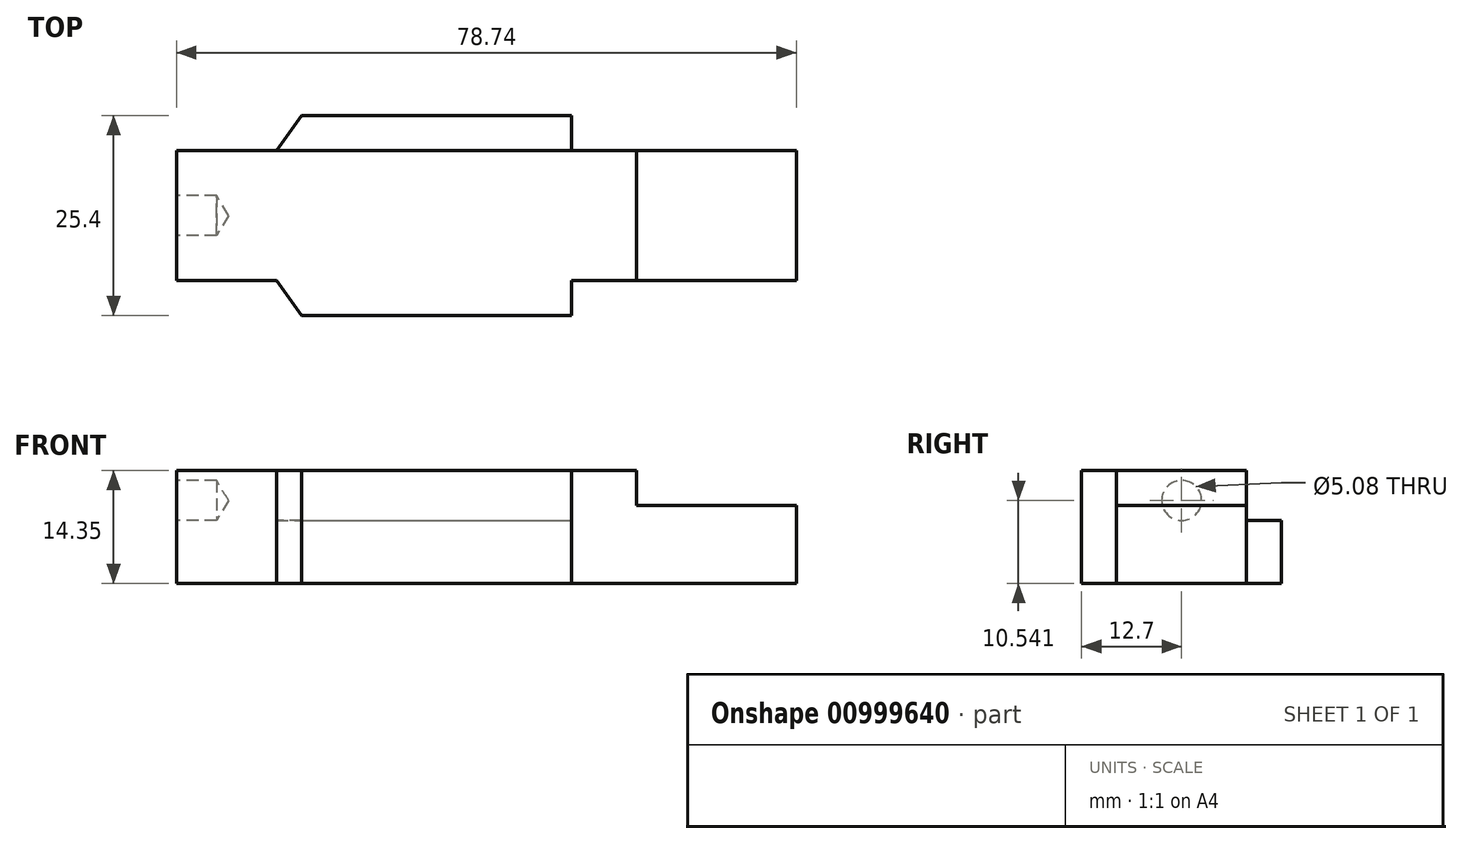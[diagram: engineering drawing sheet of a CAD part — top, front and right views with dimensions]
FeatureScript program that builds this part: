
annotation { "Feature Type Name" : "Feature", "Feature Type Description" : "" }
export const myFeature = defineFeature(function(context is Context, id is Id, definition is map)
    precondition{}
    {
        {
            var Q0;
            Q0=qCreatedBy(makeId("Front.planeOp"),FACE);
            var sketch = newSketch(context, id + "F0", { "sketchPlane" : qUnion([Q0])});
            skLineSegment(sketch, "E0", {"start": v(-39.37, 0) * mm, "end": v(-39.37, 14.35) * mm});
            skLineSegment(sketch, "E1", {"start": v(-39.37, 14.35) * mm, "end": v(19.05, 14.35) * mm});
            skLineSegment(sketch, "E2", {"start": v(19.05, 14.35) * mm, "end": v(19.05, 9.9) * mm});
            skLineSegment(sketch, "E3", {"start": v(19.05, 9.9) * mm, "end": v(39.37, 9.9) * mm});
            skLineSegment(sketch, "E4", {"start": v(39.37, 9.9) * mm, "end": v(39.37, 0) * mm});
            skLineSegment(sketch, "E5", {"start": v(39.37, 0) * mm, "end": v(-39.37, 0) * mm});
            skSolve(sketch);
        }
        {
            var Q0;
            Q0 = qSketchRegion(id + "F0", true);
            extrude(context, id + "F1", {"entities" : qUnion([Q0]), "depth" : 12.7 * mm, "offsetDistance" : 25.4 * mm, "hasSecondDirection" : true, "secondDirectionOppositeDirection" : true, "secondDirectionDepth" : 12.7 * mm});
        }
        {
            var Q0;
            Q0=makeQuery(id+"F1.opExtrude","SWEPT_FACE",FACE,{"disambiguationData":[OSD([sQuery(id+"F0.wireOp",EDGE,"E0")])]});
            var sketch = newSketch(context, id + "F2", { "sketchPlane" : qUnion([Q0])});
            skCircle(sketch, "E6", {"center": v(0, 10.54) * mm, "radius": 2.54 * mm});
            skSolve(sketch);
        }
        {
            var Q0;
            Q0=sQuery(id+"F2.wireOp",VERTEX,"E6.center");
            var Q1;
            Q1=makeQuery(id+"F1.opExtrude","SWEPT_BODY",BODY,{"disambiguationData":[OSD([sQuery(id+"F0.wireOp",EDGE,"E0"),sQuery(id+"F0.wireOp",EDGE,"E1"),sQuery(id+"F0.wireOp",EDGE,"E2"),sQuery(id+"F0.wireOp",EDGE,"E3"),sQuery(id+"F0.wireOp",EDGE,"E4"),sQuery(id+"F0.wireOp",EDGE,"E5")])]});
            hole(context, id + "F3", {"style" : HoleStyle.SIMPLE, "endStyle" : HoleEndStyle.BLIND, "holeDiameter" : 5.08 * mm, "majorDiameter" : 6.35 * mm, "holeDepth" : 5.08 * mm, "isTappedThrough" : true, "tappedDepth" : 12.7 * mm, "tapClearance" : 3, "locations" : qUnion([Q0]), "scope" : qUnion([Q1])});
        }
        {
            var Q0;
            Q0=makeQuery(id+"F1.opExtrude","SWEPT_FACE",FACE,{"disambiguationData":[OSD([sQuery(id+"F0.wireOp",EDGE,"E1")])]});
            var sketch = newSketch(context, id + "F4", { "sketchPlane" : qUnion([Q0])});
            skLineSegment(sketch, "E7", {"start": v(-39.37, 8.26) * mm, "end": v(-26.67, 8.26) * mm});
            skLineSegment(sketch, "E8", {"start": v(-26.67, 8.26) * mm, "end": v(-23.5, 12.7) * mm});
            skLineSegment(sketch, "E9", {"start": v(39.37, 8.26) * mm, "end": v(10.8, 8.26) * mm});
            skLineSegment(sketch, "E10", {"start": v(10.8, 8.26) * mm, "end": v(10.8, 12.7) * mm});
            skSolve(sketch);
        }
        {
            var Q0;
            Q0 = qSketchRegion(id + "F4", true);
            var Q1;
            Q1=makeQuery(id+"F1.opExtrude","SWEPT_FACE",FACE,{"disambiguationData":[OSD([sQuery(id+"F0.wireOp",EDGE,"E5")])]});
            var Q2;
            Q2=makeQuery(id+"F1.opExtrude","SWEPT_FACE",FACE,{"disambiguationData":[OSD([sQuery(id+"F0.wireOp",EDGE,"E5")])]});
            extrude(context, id + "F5", {"entities" : qUnion([Q0, Q1]), "operationType" : NewBodyOperationType.REMOVE, "endBound" : BoundingType.THROUGH_ALL, "depth" : 25.4 * mm, "endBoundEntityFace" : qUnion([Q2]), "offsetDistance" : 25.4 * mm});
        }
        {
            var Q0;
            {var subQ0=sQuery(id+"F4.wireOp",EDGE,"E7");Q0=makeQuery(id+"F4.imprint","IMPRINT",FACE,{"disambiguationData":[TD([[makeQuery(id+"F4.imprint","IMPRINT",EDGE,{"derivedFrom":subQ0}),1.0]])]});}
            var Q1;
            {var subQ0=sQuery(id+"F4.wireOp",EDGE,"E10");Q1=makeQuery(id+"F4.imprint","IMPRINT",FACE,{"disambiguationData":[TD([[makeQuery(id+"F4.imprint","IMPRINT",EDGE,{"derivedFrom":subQ0}),-1.0]])]});}
            extrude(context, id + "F6", {"entities" : qUnion([Q0, Q1]), "operationType" : NewBodyOperationType.REMOVE, "endBound" : BoundingType.THROUGH_ALL, "oppositeDirection" : true, "depth" : 25.4 * mm, "offsetDistance" : 25.4 * mm});
        }
        {
            var Q0;
            Q0=makeQuery(id+"F1.opExtrude","SWEPT_BODY",BODY,{"disambiguationData":[OSD([sQuery(id+"F0.wireOp",EDGE,"E0"),sQuery(id+"F0.wireOp",EDGE,"E1"),sQuery(id+"F0.wireOp",EDGE,"E2"),sQuery(id+"F0.wireOp",EDGE,"E3"),sQuery(id+"F0.wireOp",EDGE,"E4"),sQuery(id+"F0.wireOp",EDGE,"E5")])]});
            var Q1;
            Q1=qCreatedBy(makeId("Front.planeOp"),FACE);
            mirror(context, id + "F7", {"operationType" : NewBodyOperationType.INTERSECT, "entities" : qUnion([Q0]), "mirrorPlane" : qUnion([Q1])});
        }
        {
            var Q0;
            Q0=makeQuery(id+"F1.opExtrude","SWEPT_FACE",FACE,{"disambiguationData":[OSD([sQuery(id+"F0.wireOp",EDGE,"E3")])]});
            var sketch = newSketch(context, id + "F8", { "sketchPlane" : qUnion([Q0])});
            skLineSegment(sketch, "E11", {"start": v(19.05, 8.25) * mm, "end": v(39.37, 8.25) * mm});
            skLineSegment(sketch, "E12", {"start": v(19.05, -8.25) * mm, "end": v(39.37, -8.25) * mm});
            skSolve(sketch);
        }
        {
            var Q0;
            {var subQ0=sQuery(id+"F8.wireOp",EDGE,"E12");Q0=makeQuery(id+"F8.imprint","IMPRINT",FACE,{"disambiguationData":[TD([[makeQuery(id+"F8.imprint","IMPRINT",EDGE,{"derivedFrom":subQ0}),-1.0]])]});}
            var Q1;
            {var subQ0=sQuery(id+"F8.wireOp",EDGE,"E11");Q1=makeQuery(id+"F8.imprint","IMPRINT",FACE,{"disambiguationData":[TD([[makeQuery(id+"F8.imprint","IMPRINT",EDGE,{"derivedFrom":subQ0}),1.0]])]});}
            extrude(context, id + "F9", {"entities" : qUnion([Q0, Q1]), "operationType" : NewBodyOperationType.REMOVE, "endBound" : BoundingType.THROUGH_ALL, "oppositeDirection" : true, "depth" : 25.4 * mm, "offsetDistance" : 25.4 * mm});
        }
        {
            var Q0;
            Q0=makeQuery(id+"F6.boolean.opBoolean","COPY",FACE,{"derivedFrom":makeQuery(id+"F6.opExtrude","SWEPT_FACE",FACE,{"disambiguationData":[OSD([sQuery(id+"F4.wireOp",EDGE,"E10")])]})});
            var sketch = newSketch(context, id + "F10", { "sketchPlane" : qUnion([Q0])});
            skLineSegment(sketch, "E13", {"start": v(12.7, 8) * mm, "end": v(8.26, 8) * mm});
            skSolve(sketch);
        }
        {
            var Q0;
            {var subQ0=sQuery(id+"F10.wireOp",EDGE,"E13");Q0=makeQuery(id+"F10.imprint","IMPRINT",FACE,{"disambiguationData":[TD([[makeQuery(id+"F10.imprint","IMPRINT",EDGE,{"derivedFrom":subQ0}),-1.0]])]});}
            extrude(context, id + "F11", {"entities" : qUnion([Q0]), "operationType" : NewBodyOperationType.REMOVE, "endBound" : BoundingType.THROUGH_ALL, "oppositeDirection" : true, "depth" : 25.4 * mm, "offsetDistance" : 25.4 * mm});
        }
    });
